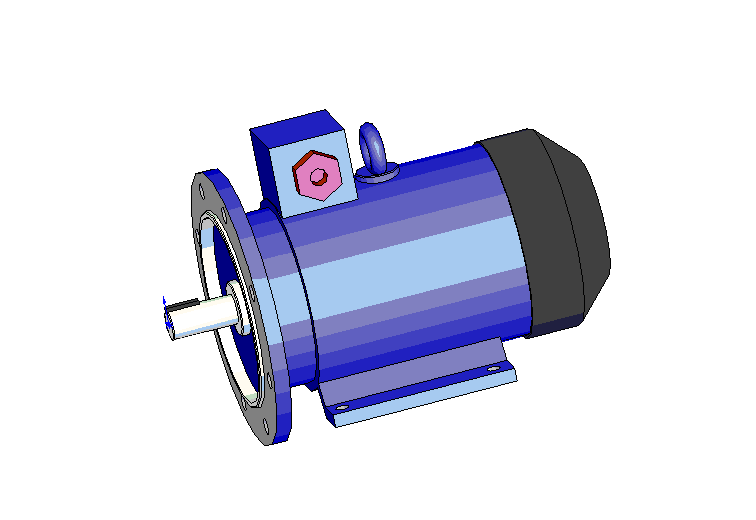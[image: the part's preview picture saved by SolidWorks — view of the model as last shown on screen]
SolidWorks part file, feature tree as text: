
SOLIDWORKS PART (.sldprt)
format: sldprt  version: not decoded by parser v0  size: 669,184 bytes
history: native  units: mm
features: sketch x18, extrude x12, plane x4, cut_extrude x4, chamfer x3, material x1, sweep x1 (+10 scaffold rows collapsed)
feature tree (53):
  scaffold x10  (default folders/planes/origin — collapsed)
  material  "Ст.3 ГОСТ 380-88"
  plane  "Спереди"
  plane  "Сверху"
  plane  "Справа"
  sketch  "Эскиз1"  dims[D1=28.0mm]
  extrude  "Вытянуть1"  Depth=60mm
  sketch  "Эскиз2"  dims[D1=7.0mm D2=7.0mm D3=31.0mm]
  extrude  "Вытянуть2"  Depth=30mm
  sketch  "Эскиз3"  dims[D1=250.0mm]
  extrude  "Вытянуть3"  Depth=14mm
  sketch  "Эскиз4"  dims[D1=180.0mm D2=170.0mm]
  extrude  "Вытянуть4"  Depth=4mm
  sketch  "Эскиз5"  dims[D1=170.0mm D2=50.0mm]
  cut_extrude  "Вырез-Вытянуть1"  Depth=8mm
  chamfer  "Фаска1"  Distance=1mm Angle=45deg
  sketch  "Эскиз6"  dims[c1.D2=15.0mm c1.D1=~135.829276mm c2.D1=22.5deg c2.D3=107.5mm c2.D4=107.5mm c2.D5=107.5mm]
  cut_extrude  "Вырез-Вытянуть2"  [1 undecoded]
  sketch  "Эскиз7"  dims[D1=160.0mm]
  extrude  "Вытянуть5"  Depth=37mm
  sketch  "Эскиз8"  dims[D1=176.0mm]
  extrude  "Вытянуть6"  Depth=197mm
  sketch  "Эскиз9"  dims[D1=180.0mm]
  extrude  "Вытянуть7"  Depth=83mm
  chamfer  "Фаска2"  Distance=35mm Angle=45deg
  sketch  "Эскиз10"  dims[c1.D1=12.0mm c1.D2=94.0mm c1.D3=28.0mm c1.D4=~55.466073mm c2.D4=~177.155724deg c3.D4=10.0mm c3.D5=~54.33349mm c4.D5=30.0deg c4.D6=100.0mm]
  extrude  "Вытянуть8"  Depth=168mm
  sketch  "Эскиз11"  dims[c1.D2=12.0mm c1.D1=123.0mm c1.D3=80.0mm c1.D4=90.0deg c1.D5=160.0mm c1.D6=140.0mm c1.D7=140.0mm c1.D8=235.0mm c2.D4=~157.853288mm c3.D4=90.0deg c3.D6=140.0mm c3.D3=80.0mm c4.D4=90.0deg c4.D5=263.0mm c4.D6=160.0mm c4.D7=140.0mm]
  cut_extrude  "Вырез-Вытянуть3"  [1 undecoded]
  sketch  "Эскиз12"  dims[D1=70.0mm D2=70.0mm D3=1.0mm]
  extrude  "Вытянуть9"  Depth=146.5mm
  sketch  "Эскиз13"  dims[c1.D1=~21.871095mm c1.D2=40.0mm c2.D1=210.0mm]
  extrude  "Вытянуть10"  Depth=92.5mm
  chamfer  "Фаска3"  Distance=1mm Angle=45deg
  plane  "Плоскость1"  Offset=210mm
  sketch  "Эскиз14"  dims[D1=36.0mm]
  sketch  "Эскиз15"  dims[D1=14.0mm D2=36.0mm]
  sweep  "По траектории1"
  sketch  "Эскиз16"  dims[D1=30.0mm D2=30.0mm D3=35.0mm]
  extrude  "Вытянуть11"  Depth=10mm
  sketch  "Эскиз17"  dims[D1=~34.383632mm]
  extrude  "Вытянуть12"  Depth=12mm
  sketch  "Эскиз18"  dims[D1=16.0mm]
  cut_extrude  "Вырез-Вытянуть4"  Depth=12mm
decode coverage: 35 of 38 modeling features carry decoded parameters
note: ~ marks probable driven/reference dimensions
note: 2 parameter values undecoded
note: suppression state not decoded; provenance and decode notes live in map.json
